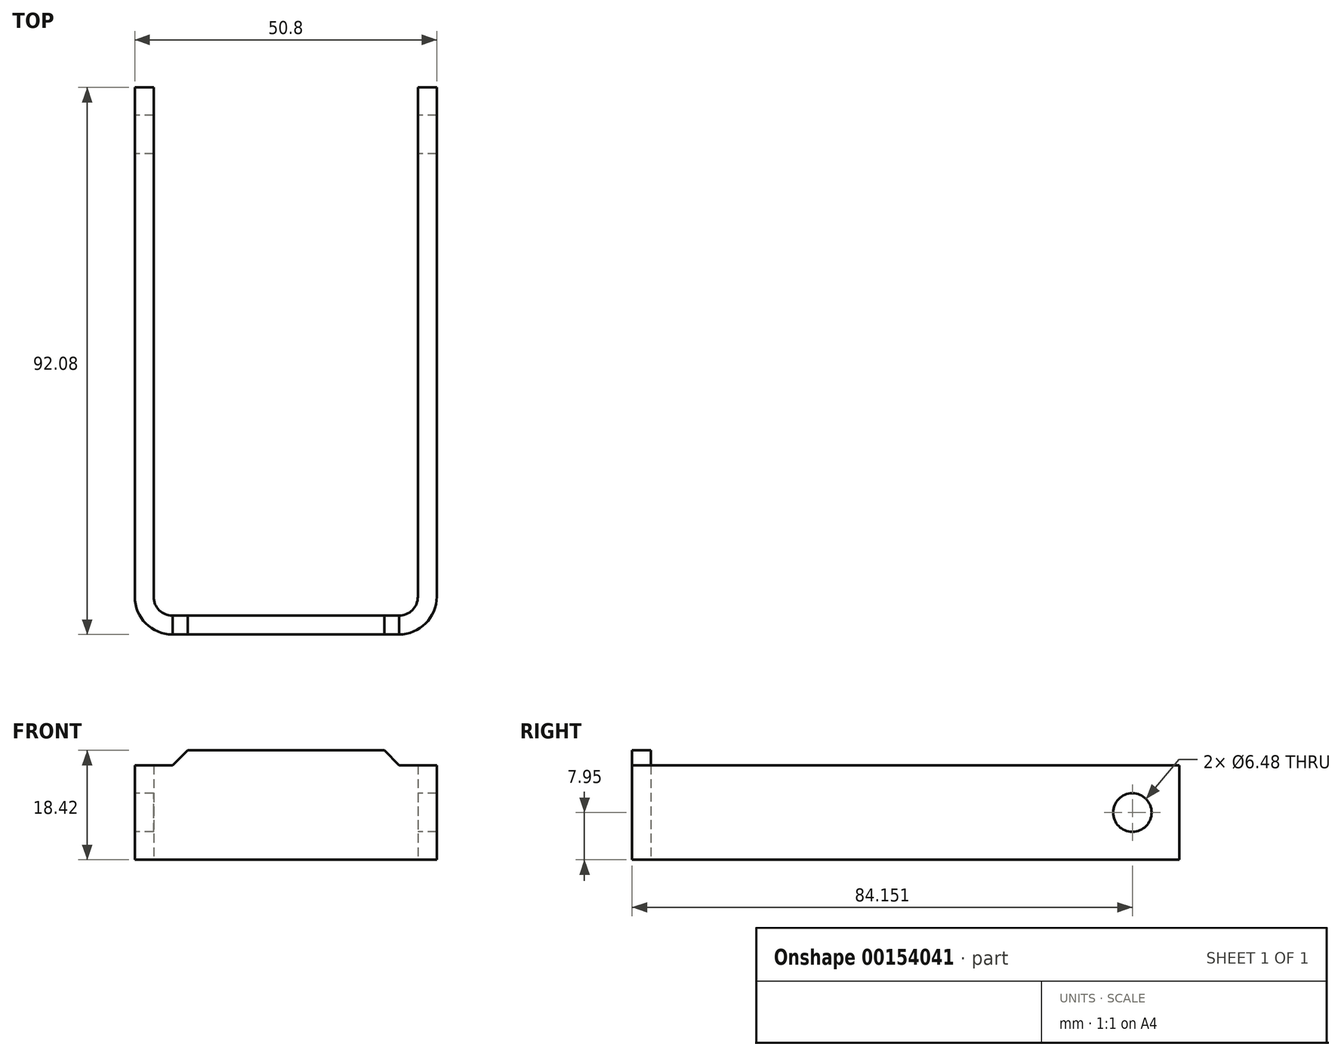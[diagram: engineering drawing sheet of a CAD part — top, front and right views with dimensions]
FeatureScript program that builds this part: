
annotation { "Feature Type Name" : "Feature", "Feature Type Description" : "" }
export const myFeature = defineFeature(function(context is Context, id is Id, definition is map)
    precondition{}
    {
        {
            var Q0;
            Q0=qCreatedBy(makeId("Top.planeOp"),FACE);
            var sketch = newSketch(context, id + "F0", { "sketchPlane" : qUnion([Q0])});
            skLineSegment(sketch, "E0", {"start": v(-46.18, 50.4) * mm, "end": v(-46.18, -35.33) * mm});
            skLineSegment(sketch, "E1", {"start": v(-39.83, -41.68) * mm, "end": v(-1.73, -41.68) * mm});
            skLineSegment(sketch, "E2", {"start": v(4.62, -35.33) * mm, "end": v(4.62, 50.4) * mm});
            skPoint(sketch, "E3.visualSharp", {"position": v(-46.18, -41.68) * mm});
            skArc(sketch, "E3.filletArc", {"start": v(-46.18, -35.33) * mm, "mid": v(-44.32, -39.82) * mm, "end": v(-39.83, -41.68) * mm});
            skPoint(sketch, "E4.visualSharp", {"position": v(4.62, -41.68) * mm});
            skArc(sketch, "E4.filletArc", {"start": v(-1.73, -41.68) * mm, "mid": v(2.76, -39.82) * mm, "end": v(4.62, -35.33) * mm});
            skLineSegment(sketch, "E5.0", {"start": v(1.44, -35.33) * mm, "end": v(1.44, 50.4) * mm});
            skLineSegment(sketch, "E5.1", {"start": v(-39.83, -38.5) * mm, "end": v(-1.73, -38.5) * mm});
            skLineSegment(sketch, "E5.2", {"start": v(-43, 50.4) * mm, "end": v(-43, -35.33) * mm});
            skPoint(sketch, "E6.visualSharp", {"position": v(-43, -38.5) * mm});
            skArc(sketch, "E6.filletArc", {"start": v(-43, -35.33) * mm, "mid": v(-42.08, -37.57) * mm, "end": v(-39.83, -38.5) * mm});
            skPoint(sketch, "E7.visualSharp", {"position": v(1.44, -38.5) * mm});
            skArc(sketch, "E7.filletArc", {"start": v(-1.73, -38.5) * mm, "mid": v(0.51, -37.57) * mm, "end": v(1.44, -35.33) * mm});
            skLineSegment(sketch, "E8", {"start": v(-46.18, 50.4) * mm, "end": v(-43, 50.4) * mm});
            skLineSegment(sketch, "E9", {"start": v(1.44, 50.4) * mm, "end": v(4.62, 50.4) * mm});
            skLineSegment(sketch, "E10", {"start": v(-39.83, -41.68) * mm, "end": v(-39.83, -38.5) * mm});
            skLineSegment(sketch, "E11", {"start": v(-1.73, -38.5) * mm, "end": v(-1.73, -41.68) * mm});
            skSolve(sketch);
        }
        {
            var Q0;
            Q0=makeQuery(id+"F0.imprint","IMPRINT",FACE,{"disambiguationData":[TD([[makeQuery(id+"F0.imprint","IMPRINT",EDGE,{"derivedFrom":sQuery(id+"F0.wireOp",EDGE,"E0")}),1.0]])]});
            var Q1;
            Q1=makeQuery(id+"F0.imprint","IMPRINT",FACE,{"disambiguationData":[TD([[makeQuery(id+"F0.imprint","IMPRINT",EDGE,{"derivedFrom":sQuery(id+"F0.wireOp",EDGE,"E1")}),1.0]])]});
            var Q2;
            Q2=makeQuery(id+"F0.imprint","IMPRINT",FACE,{"disambiguationData":[TD([[makeQuery(id+"F0.imprint","IMPRINT",EDGE,{"derivedFrom":sQuery(id+"F0.wireOp",EDGE,"E2")}),1.0]])]});
            extrude(context, id + "F1", {"entities" : qUnion([Q0, Q1, Q2]), "depth" : 15.88 * mm});
        }
        {
            var Q0;
            Q0=makeQuery(id+"F1.opExtrude","CAP_FACE",FACE,{"disambiguationData":[OSD([sQuery(id+"F0.wireOp",EDGE,"E0"),sQuery(id+"F0.wireOp",EDGE,"E1"),sQuery(id+"F0.wireOp",EDGE,"E2"),sQuery(id+"F0.wireOp",EDGE,"E3.filletArc"),sQuery(id+"F0.wireOp",EDGE,"E4.filletArc"),sQuery(id+"F0.wireOp",EDGE,"E5.0"),sQuery(id+"F0.wireOp",EDGE,"E5.1"),sQuery(id+"F0.wireOp",EDGE,"E5.2"),sQuery(id+"F0.wireOp",EDGE,"E6.filletArc"),sQuery(id+"F0.wireOp",EDGE,"E7.filletArc"),sQuery(id+"F0.wireOp",EDGE,"E8"),sQuery(id+"F0.wireOp",EDGE,"E9")])],"isStart":false});
            var sketch = newSketch(context, id + "F2", { "sketchPlane" : qUnion([Q0])});
            skLineSegment(sketch, "E12", {"start": v(-39.83, -38.5) * mm, "end": v(-39.83, -41.68) * mm});
            skLineSegment(sketch, "E13", {"start": v(-39.83, -41.68) * mm, "end": v(-1.73, -41.68) * mm});
            skLineSegment(sketch, "E14", {"start": v(-1.73, -41.68) * mm, "end": v(-1.73, -38.5) * mm});
            skLineSegment(sketch, "E15", {"start": v(-1.73, -38.5) * mm, "end": v(-39.83, -38.5) * mm});
            skSolve(sketch);
        }
        {
            var Q0;
            Q0=makeQuery(id+"F2.imprint","IMPRINT",FACE,{"disambiguationData":[TD([[makeQuery(id+"F2.imprint","IMPRINT",EDGE,{"derivedFrom":sQuery(id+"F2.wireOp",EDGE,"E12")}),1.0]])]});
            extrude(context, id + "F3", {"entities" : qUnion([Q0]), "operationType" : NewBodyOperationType.ADD, "depth" : 2.54 * mm});
        }
        {
            var Q0;
            Q0=makeQuery(id+"F3.boolean.opBoolean","MERGE",FACE,{"derivedFrom":[makeQuery(id+"F1.opExtrude","SWEPT_FACE",FACE,{"disambiguationData":[OSD([sQuery(id+"F0.wireOp",EDGE,"E1")])]}),makeQuery(id+"F3.opExtrude","SWEPT_FACE",FACE,{"disambiguationData":[OSD([sQuery(id+"F2.wireOp",EDGE,"E13")])]})]});
            var sketch = newSketch(context, id + "F4", { "sketchPlane" : qUnion([Q0])});
            skLineSegment(sketch, "E16", {"start": v(-39.83, 15.88) * mm, "end": v(-37.3, 18.41) * mm});
            skLineSegment(sketch, "E17", {"start": v(-4.2, 18.41) * mm, "end": v(-1.73, 18.41) * mm});
            skLineSegment(sketch, "E18", {"start": v(-39.83, 15.88) * mm, "end": v(-39.83, 18.41) * mm});
            skLineSegment(sketch, "E19", {"start": v(-39.83, 18.41) * mm, "end": v(-37.3, 18.41) * mm});
            skLineSegment(sketch, "E20", {"start": v(-4.2, 18.41) * mm, "end": v(-1.73, 15.88) * mm});
            skLineSegment(sketch, "E21", {"start": v(-1.73, 15.88) * mm, "end": v(-1.73, 18.41) * mm});
            skSolve(sketch);
        }
        {
            var Q0;
            Q0=makeQuery(id+"F4.imprint","IMPRINT",FACE,{"disambiguationData":[TD([[makeQuery(id+"F4.imprint","IMPRINT",EDGE,{"derivedFrom":sQuery(id+"F4.wireOp",EDGE,"E16")}),1.0]])]});
            var Q1;
            Q1=makeQuery(id+"F4.imprint","IMPRINT",FACE,{"disambiguationData":[TD([[makeQuery(id+"F4.imprint","IMPRINT",EDGE,{"derivedFrom":sQuery(id+"F4.wireOp",EDGE,"E17")}),-1.0]])]});
            extrude(context, id + "F5", {"entities" : qUnion([Q0, Q1]), "operationType" : NewBodyOperationType.REMOVE, "oppositeDirection" : true, "depth" : 25.4 * mm});
        }
        {
            var Q0;
            Q0=makeQuery(id+"F1.opExtrude","SWEPT_FACE",FACE,{"disambiguationData":[OSD([sQuery(id+"F0.wireOp",EDGE,"E0")])]});
            var sketch = newSketch(context, id + "F6", { "sketchPlane" : qUnion([Q0])});
            skCircle(sketch, "E22", {"center": v(-42.47, 7.95) * mm, "radius": 3.24 * mm});
            skSolve(sketch);
        }
        {
            var Q0;
            Q0 = qSketchRegion(id + "F6", true);
            extrude(context, id + "F7", {"entities" : qUnion([Q0]), "operationType" : NewBodyOperationType.REMOVE, "oppositeDirection" : true, "depth" : 101.6 * mm});
        }
    });
